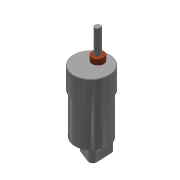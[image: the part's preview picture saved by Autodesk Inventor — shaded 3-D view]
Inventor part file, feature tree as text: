
AUTODESK INVENTOR PART (.ipt)
format: ipt  version: 2013 (Build 170138000, 138)  size: 218,112 bytes
history: native  units: in
note: dims shown in document units (in); Inventor stores cm internally (conversion verified against a paired STEP export)
features: other x4, sketch x4
ambient origin geometry x8: Origin, YZ Plane, XZ Plane, XY Plane, X Axis, Y Axis, Z Axis, Center Point
bodies: Solid1 (feature_tree), Solid2 (feature_tree)
feature tree (8):
  other  "Tetrix motor.ipt"
  other  "DC_MOTOR_2011::Tetrix motor.ipt"
  other  "Solid2::Tetrix motor.ipt"
  other  "TaggingFeature1"
  sketch  "Sketch1"  dims[d0=0.3937in]
  sketch  "Sketch2"  dims[d1=0.5909in d3=0.3436in d5=0.4528in d6=0.4528in d7=0.1654in d8=0.0in d9=0.748in d11=0.4331in d12=0.3661in d13=0.0in d14=0.2165in d16=0.0472in d17=0.0in d18=0.0197in d19=0.0787in d20=0.1181in d21=0.1181in d22=0.5906in d23=0.0in]
  sketch  "Sketch3"
  sketch  "Sketch4"
